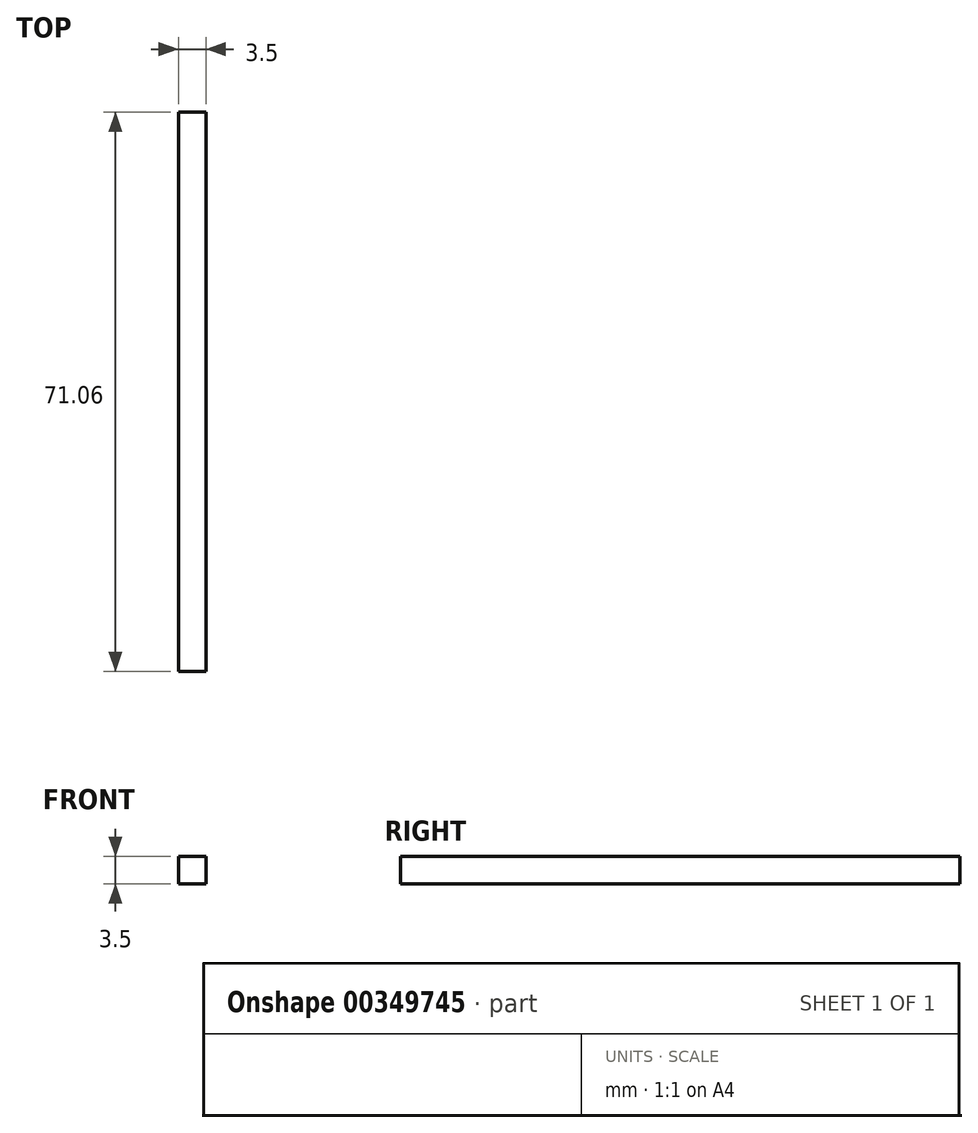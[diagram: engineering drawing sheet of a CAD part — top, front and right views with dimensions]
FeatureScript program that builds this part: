
annotation { "Feature Type Name" : "Feature", "Feature Type Description" : "" }
export const myFeature = defineFeature(function(context is Context, id is Id, definition is map)
    precondition{}
    {
        {
            var Q0;
            Q0=qCreatedBy(makeId("Top.planeOp"),FACE);
            var sketch = newSketch(context, id + "F0", { "sketchPlane" : qUnion([Q0])});
            skLineSegment(sketch, "E0.bottom", {"start": v(1.75, -35.53) * mm, "end": v(-1.75, -35.53) * mm});
            skLineSegment(sketch, "E0.top", {"start": v(1.75, 35.53) * mm, "end": v(-1.75, 35.53) * mm});
            skLineSegment(sketch, "E0.left", {"start": v(1.75, -35.53) * mm, "end": v(1.75, 35.53) * mm});
            skLineSegment(sketch, "E0.right", {"start": v(-1.75, -35.53) * mm, "end": v(-1.75, 35.53) * mm});
            skPoint(sketch, "E0.middle", {"position": v(0, 0) * mm});
            skSolve(sketch);
        }
        {
            var Q0;
            Q0=qSketchRegion(id+"F0",true);
            extrude(context, id + "F1", {"entities" : qUnion([Q0]), "depth" : 3.5 * mm});
        }
    });
